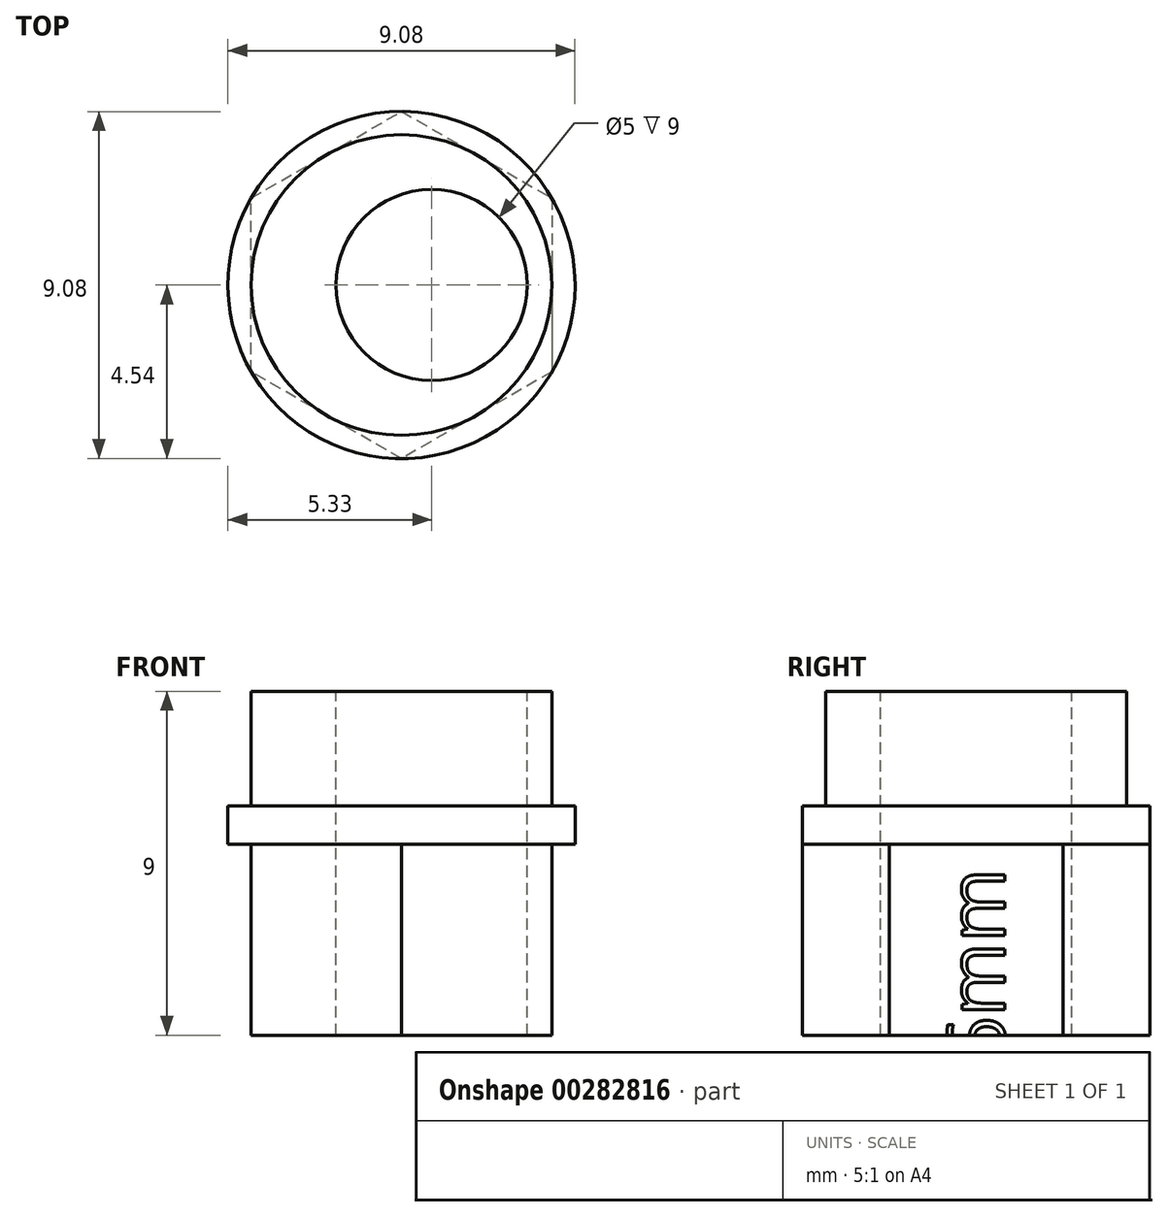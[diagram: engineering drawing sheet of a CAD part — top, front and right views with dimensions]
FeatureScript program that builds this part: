
annotation { "Feature Type Name" : "Feature", "Feature Type Description" : "" }
export const myFeature = defineFeature(function(context is Context, id is Id, definition is map)
    precondition{}
    {
        {
            var Q0;
            Q0=qCreatedBy(makeId("Top.planeOp"),FACE);
            var sketch = newSketch(context, id + "F0", { "sketchPlane" : qUnion([Q0])});
            skCircle(sketch, "E0", {"center": v(0, 0) * mm, "radius": 3.94 * mm});
            skCircle(sketch, "E1.cCircle", {"center": v(0, 0) * mm, "radius": 3.94 * mm, "construction": true});
            skLineSegment(sketch, "E1.0", {"start": v(-3.94, 2.27) * mm, "end": v(0, 4.54) * mm});
            skLineSegment(sketch, "E1.1", {"start": v(0, 4.54) * mm, "end": v(3.94, 2.27) * mm});
            skLineSegment(sketch, "E1.2", {"start": v(3.94, 2.27) * mm, "end": v(3.94, -2.27) * mm});
            skLineSegment(sketch, "E1.3", {"start": v(3.94, -2.27) * mm, "end": v(0, -4.54) * mm});
            skLineSegment(sketch, "E1.4", {"start": v(0, -4.54) * mm, "end": v(-3.94, -2.27) * mm});
            skLineSegment(sketch, "E1.5", {"start": v(-3.94, -2.27) * mm, "end": v(-3.94, 2.27) * mm});
            skPoint(sketch, "E1.0.midPoint", {"position": v(-1.97, 3.4) * mm});
            skCircle(sketch, "E2", {"center": v(0.79, 0) * mm, "radius": 2.5 * mm});
            skCircle(sketch, "E3", {"center": v(0, 0) * mm, "radius": 4.54 * mm});
            skSolve(sketch);
        }
        {
            var Q0;
            {var subQ0=sQuery(id+"F0.wireOp",EDGE,"E1.5");var subQ1=sQuery(id+"F0.wireOp",EDGE,"E0");var subQ2=makeQuery(id+"F0.imprint","INTERSECT",VERTEX,{"derivedFrom":[subQ1,subQ0]});Q0=makeQuery(id+"F0.imprint","IMPRINT",FACE,{"disambiguationData":[TD([[makeQuery(id+"F0.imprint","IMPRINT",EDGE,{"disambiguationData":[TD([[subQ2,-1.0]])],"derivedFrom":subQ1}),-1.0]])]});}
            var Q1;
            {var subQ0=sQuery(id+"F0.wireOp",EDGE,"E1.0");var subQ1=sQuery(id+"F0.wireOp",EDGE,"E0");var subQ2=makeQuery(id+"F0.imprint","INTERSECT",VERTEX,{"derivedFrom":[subQ1,subQ0]});Q1=makeQuery(id+"F0.imprint","IMPRINT",FACE,{"disambiguationData":[TD([[makeQuery(id+"F0.imprint","IMPRINT",EDGE,{"disambiguationData":[TD([[subQ2,-1.0]])],"derivedFrom":subQ1}),-1.0]])]});}
            var Q2;
            {var subQ0=sQuery(id+"F0.wireOp",EDGE,"E1.1");var subQ1=sQuery(id+"F0.wireOp",EDGE,"E0");var subQ2=makeQuery(id+"F0.imprint","INTERSECT",VERTEX,{"derivedFrom":[subQ1,subQ0]});Q2=makeQuery(id+"F0.imprint","IMPRINT",FACE,{"disambiguationData":[TD([[makeQuery(id+"F0.imprint","IMPRINT",EDGE,{"disambiguationData":[TD([[subQ2,-1.0]])],"derivedFrom":subQ1}),-1.0]])]});}
            var Q3;
            {var subQ0=sQuery(id+"F0.wireOp",EDGE,"E1.1");var subQ1=sQuery(id+"F0.wireOp",EDGE,"E0");var subQ2=makeQuery(id+"F0.imprint","INTERSECT",VERTEX,{"derivedFrom":[subQ1,subQ0]});Q3=makeQuery(id+"F0.imprint","IMPRINT",FACE,{"disambiguationData":[TD([[makeQuery(id+"F0.imprint","IMPRINT",EDGE,{"disambiguationData":[TD([[subQ2,1.0]])],"derivedFrom":subQ1}),-1.0]])]});}
            var Q4;
            {var subQ0=sQuery(id+"F0.wireOp",EDGE,"E1.2");var subQ1=sQuery(id+"F0.wireOp",EDGE,"E0");var subQ2=makeQuery(id+"F0.imprint","INTERSECT",VERTEX,{"derivedFrom":[subQ1,subQ0]});Q4=makeQuery(id+"F0.imprint","IMPRINT",FACE,{"disambiguationData":[TD([[makeQuery(id+"F0.imprint","IMPRINT",EDGE,{"disambiguationData":[TD([[subQ2,1.0]])],"derivedFrom":subQ1}),-1.0]])]});}
            var Q5;
            {var subQ0=sQuery(id+"F0.wireOp",EDGE,"E1.4");var subQ1=sQuery(id+"F0.wireOp",EDGE,"E0");var subQ2=makeQuery(id+"F0.imprint","INTERSECT",VERTEX,{"derivedFrom":[subQ1,subQ0]});Q5=makeQuery(id+"F0.imprint","IMPRINT",FACE,{"disambiguationData":[TD([[makeQuery(id+"F0.imprint","IMPRINT",EDGE,{"disambiguationData":[TD([[subQ2,-1.0]])],"derivedFrom":subQ1}),-1.0]])]});}
            var Q6;
            Q6=makeQuery(id+"F0.imprint","IMPRINT",FACE,{"disambiguationData":[TD([[makeQuery(id+"F0.imprint","IMPRINT",EDGE,{"derivedFrom":sQuery(id+"F0.wireOp",EDGE,"E2")}),-1.0]])]});
            extrude(context, id + "F1", {"entities" : qUnion([Q0, Q1, Q2, Q3, Q4, Q5, Q6]), "oppositeDirection" : true, "depth" : 5 * mm});
        }
        {
            var Q0;
            Q0=makeQuery(id+"F0.imprint","IMPRINT",FACE,{"disambiguationData":[TD([[makeQuery(id+"F0.imprint","IMPRINT",EDGE,{"derivedFrom":sQuery(id+"F0.wireOp",EDGE,"E2")}),-1.0]])]});
            var Q1;
            {var subQ1=sQuery(id+"F0.wireOp",EDGE,"E1.4");var subQ3=makeQuery(id+"F0.imprint","INTERSECT",VERTEX,{"derivedFrom":[sQuery(id+"F0.wireOp",EDGE,"E0"),subQ1]});Q1=makeQuery(id+"F0.imprint","IMPRINT",FACE,{"disambiguationData":[TD([[makeQuery(id+"F0.imprint","IMPRINT",EDGE,{"disambiguationData":[TD([[subQ3,1.0]])],"derivedFrom":subQ1}),1.0]])]});}
            var Q2;
            {var subQ0=sQuery(id+"F0.wireOp",EDGE,"E1.4");var subQ1=sQuery(id+"F0.wireOp",EDGE,"E0");var subQ2=makeQuery(id+"F0.imprint","INTERSECT",VERTEX,{"derivedFrom":[subQ1,subQ0]});Q2=makeQuery(id+"F0.imprint","IMPRINT",FACE,{"disambiguationData":[TD([[makeQuery(id+"F0.imprint","IMPRINT",EDGE,{"disambiguationData":[TD([[subQ2,-1.0]])],"derivedFrom":subQ1}),-1.0]])]});}
            var Q3;
            {var subQ1=sQuery(id+"F0.wireOp",EDGE,"E1.3");var subQ3=makeQuery(id+"F0.imprint","INTERSECT",VERTEX,{"derivedFrom":[sQuery(id+"F0.wireOp",EDGE,"E0"),subQ1]});Q3=makeQuery(id+"F0.imprint","IMPRINT",FACE,{"disambiguationData":[TD([[makeQuery(id+"F0.imprint","IMPRINT",EDGE,{"disambiguationData":[TD([[subQ3,1.0]])],"derivedFrom":subQ1}),1.0]])]});}
            var Q4;
            {var subQ0=sQuery(id+"F0.wireOp",EDGE,"E1.2");var subQ1=sQuery(id+"F0.wireOp",EDGE,"E0");var subQ2=makeQuery(id+"F0.imprint","INTERSECT",VERTEX,{"derivedFrom":[subQ1,subQ0]});Q4=makeQuery(id+"F0.imprint","IMPRINT",FACE,{"disambiguationData":[TD([[makeQuery(id+"F0.imprint","IMPRINT",EDGE,{"disambiguationData":[TD([[subQ2,1.0]])],"derivedFrom":subQ1}),-1.0]])]});}
            var Q5;
            {var subQ1=sQuery(id+"F0.wireOp",EDGE,"E1.2");var subQ3=makeQuery(id+"F0.imprint","INTERSECT",VERTEX,{"derivedFrom":[sQuery(id+"F0.wireOp",EDGE,"E0"),subQ1]});Q5=makeQuery(id+"F0.imprint","IMPRINT",FACE,{"disambiguationData":[TD([[makeQuery(id+"F0.imprint","IMPRINT",EDGE,{"disambiguationData":[TD([[subQ3,1.0]])],"derivedFrom":subQ1}),1.0]])]});}
            var Q6;
            {var subQ0=sQuery(id+"F0.wireOp",EDGE,"E1.1");var subQ1=sQuery(id+"F0.wireOp",EDGE,"E0");var subQ2=makeQuery(id+"F0.imprint","INTERSECT",VERTEX,{"derivedFrom":[subQ1,subQ0]});Q6=makeQuery(id+"F0.imprint","IMPRINT",FACE,{"disambiguationData":[TD([[makeQuery(id+"F0.imprint","IMPRINT",EDGE,{"disambiguationData":[TD([[subQ2,1.0]])],"derivedFrom":subQ1}),-1.0]])]});}
            var Q7;
            {var subQ1=sQuery(id+"F0.wireOp",EDGE,"E1.1");var subQ3=makeQuery(id+"F0.imprint","INTERSECT",VERTEX,{"derivedFrom":[sQuery(id+"F0.wireOp",EDGE,"E0"),subQ1]});Q7=makeQuery(id+"F0.imprint","IMPRINT",FACE,{"disambiguationData":[TD([[makeQuery(id+"F0.imprint","IMPRINT",EDGE,{"disambiguationData":[TD([[subQ3,1.0]])],"derivedFrom":subQ1}),1.0]])]});}
            var Q8;
            {var subQ0=sQuery(id+"F0.wireOp",EDGE,"E1.1");var subQ1=sQuery(id+"F0.wireOp",EDGE,"E0");var subQ2=makeQuery(id+"F0.imprint","INTERSECT",VERTEX,{"derivedFrom":[subQ1,subQ0]});Q8=makeQuery(id+"F0.imprint","IMPRINT",FACE,{"disambiguationData":[TD([[makeQuery(id+"F0.imprint","IMPRINT",EDGE,{"disambiguationData":[TD([[subQ2,-1.0]])],"derivedFrom":subQ1}),-1.0]])]});}
            var Q9;
            {var subQ1=sQuery(id+"F0.wireOp",EDGE,"E1.0");var subQ3=makeQuery(id+"F0.imprint","INTERSECT",VERTEX,{"derivedFrom":[sQuery(id+"F0.wireOp",EDGE,"E0"),subQ1]});Q9=makeQuery(id+"F0.imprint","IMPRINT",FACE,{"disambiguationData":[TD([[makeQuery(id+"F0.imprint","IMPRINT",EDGE,{"disambiguationData":[TD([[subQ3,1.0]])],"derivedFrom":subQ1}),1.0]])]});}
            var Q10;
            {var subQ0=sQuery(id+"F0.wireOp",EDGE,"E1.0");var subQ1=sQuery(id+"F0.wireOp",EDGE,"E0");var subQ2=makeQuery(id+"F0.imprint","INTERSECT",VERTEX,{"derivedFrom":[subQ1,subQ0]});Q10=makeQuery(id+"F0.imprint","IMPRINT",FACE,{"disambiguationData":[TD([[makeQuery(id+"F0.imprint","IMPRINT",EDGE,{"disambiguationData":[TD([[subQ2,-1.0]])],"derivedFrom":subQ1}),-1.0]])]});}
            var Q11;
            {var subQ1=sQuery(id+"F0.wireOp",EDGE,"E1.5");var subQ3=makeQuery(id+"F0.imprint","INTERSECT",VERTEX,{"derivedFrom":[sQuery(id+"F0.wireOp",EDGE,"E0"),subQ1]});Q11=makeQuery(id+"F0.imprint","IMPRINT",FACE,{"disambiguationData":[TD([[makeQuery(id+"F0.imprint","IMPRINT",EDGE,{"disambiguationData":[TD([[subQ3,1.0]])],"derivedFrom":subQ1}),1.0]])]});}
            var Q12;
            {var subQ0=sQuery(id+"F0.wireOp",EDGE,"E1.5");var subQ1=sQuery(id+"F0.wireOp",EDGE,"E0");var subQ2=makeQuery(id+"F0.imprint","INTERSECT",VERTEX,{"derivedFrom":[subQ1,subQ0]});Q12=makeQuery(id+"F0.imprint","IMPRINT",FACE,{"disambiguationData":[TD([[makeQuery(id+"F0.imprint","IMPRINT",EDGE,{"disambiguationData":[TD([[subQ2,-1.0]])],"derivedFrom":subQ1}),-1.0]])]});}
            extrude(context, id + "F2", {"entities" : qUnion([Q0, Q1, Q2, Q3, Q4, Q5, Q6, Q7, Q8, Q9, Q10, Q11, Q12]), "operationType" : NewBodyOperationType.ADD, "depth" : 1 * mm});
        }
        {
            var Q0;
            Q0=makeQuery(id+"F0.imprint","IMPRINT",FACE,{"disambiguationData":[TD([[makeQuery(id+"F0.imprint","IMPRINT",EDGE,{"derivedFrom":sQuery(id+"F0.wireOp",EDGE,"E2")}),-1.0]])]});
            extrude(context, id + "F3", {"entities" : qUnion([Q0]), "operationType" : NewBodyOperationType.ADD, "depth" : 4 * mm});
        }
        {
            var Q0;
            Q0=makeQuery(id+"F1.opExtrude","SWEPT_FACE",FACE,{"disambiguationData":[OSD([sQuery(id+"F0.wireOp",EDGE,"E1.2")])]});
            var sketch = newSketch(context, id + "F4", { "sketchPlane" : qUnion([Q0])});
            skText(sketch, "E4", { "text": "6mm", "fontName": "OpenSans-Regular.ttf"});
            skPoint(sketch, "E5", {"position": v(0, 0.02) * mm});
            const initialGuessF4  = {"E4": [0.00075, -0.0057, 0, 1, 0.0015]};
            skSetInitialGuess(sketch, initialGuessF4);
            skSolve(sketch);
        }
        {
            var Q0;
            Q0=qSketchRegion(id+"F4",true);
            extrude(context, id + "F5", {"entities" : qUnion([Q0]), "operationType" : NewBodyOperationType.REMOVE, "oppositeDirection" : true, "depth" : 0.01 * mm});
        }
    });
